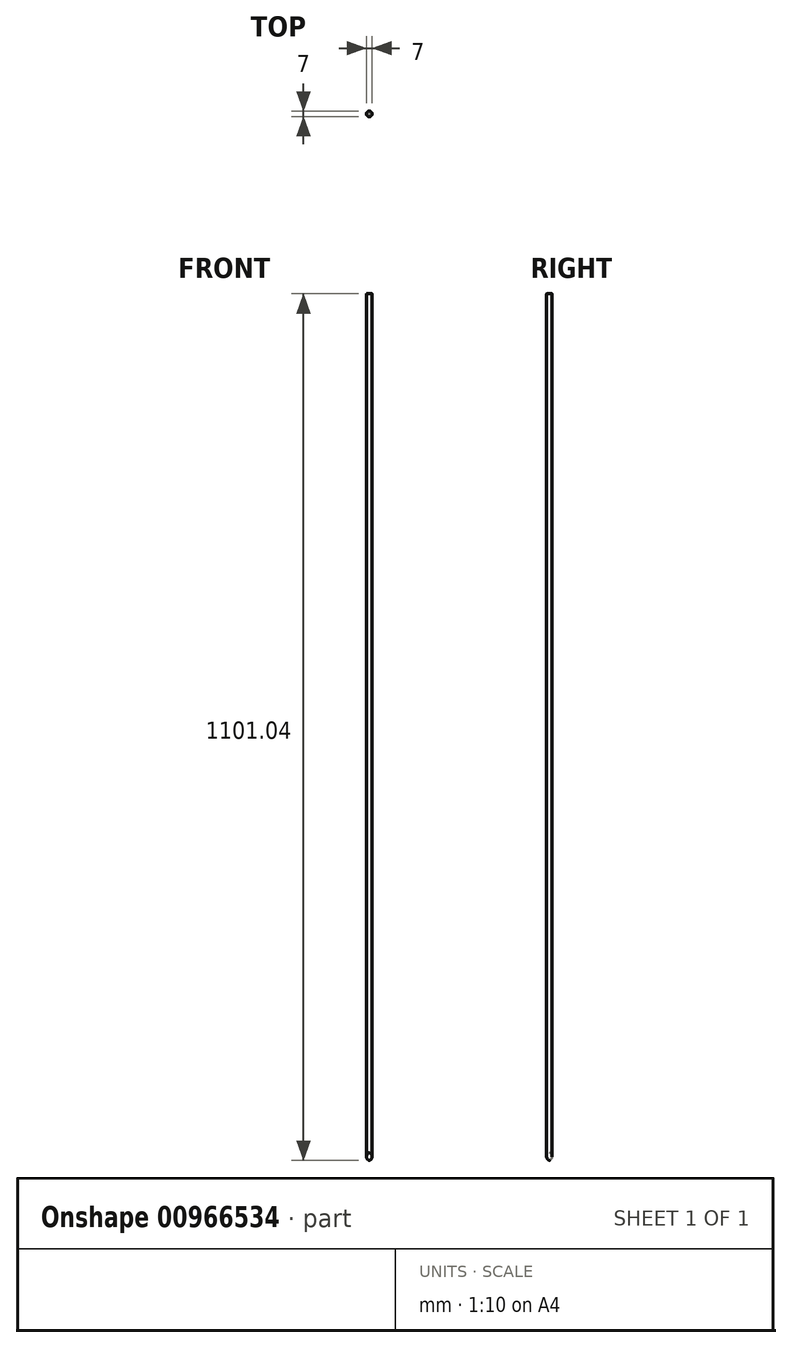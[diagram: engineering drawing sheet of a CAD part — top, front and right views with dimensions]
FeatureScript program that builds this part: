
annotation { "Feature Type Name" : "Feature", "Feature Type Description" : "" }
export const myFeature = defineFeature(function(context is Context, id is Id, definition is map)
    precondition{}
    {
        {
            var Q0;
            Q0=qCreatedBy(makeId("Right.planeOp"),FACE);
            var sketch = newSketch(context, id + "F0", { "sketchPlane" : qUnion([Q0])});
            skLineSegment(sketch, "E0", {"start": v(3.5, 1099.66) * mm, "end": v(3.5, 3.77) * mm});
            skLineSegment(sketch, "E1", {"start": v(0, -1) * mm, "end": v(-0.13, -1.04) * mm});
            skLineSegment(sketch, "E2", {"start": v(0, -1) * mm, "end": v(0, 1100) * mm});
            skLineSegment(sketch, "E3", {"start": v(0, 1100) * mm, "end": v(3.16, 1100) * mm});
            skPoint(sketch, "E4.visualSharp", {"position": v(3.5, 0) * mm});
            skArc(sketch, "E4.filletArc", {"start": v(-0.13, -1.04) * mm, "mid": v(2.5, 0.76) * mm, "end": v(3.5, 3.77) * mm});
            skPoint(sketch, "E5.visualSharp", {"position": v(3.5, 1100) * mm});
            skArc(sketch, "E5.filletArc", {"start": v(3.5, 1099.66) * mm, "mid": v(3.4, 1099.9) * mm, "end": v(3.16, 1100) * mm});
            skSolve(sketch);
        }
        {
            var Q0;
            Q0 = qSketchRegion(id + "F0", true);
            var Q1;
            Q1=sQuery(id+"F0.wireOp",EDGE,"E2");
            revolve(context, id + "F1", {"surfaceOperationType" : NewSurfaceOperationType.NEW, "entities" : qUnion([Q0]), "axis" : qUnion([Q1]), "revolveType" : RevolveType.FULL});
        }
    });
